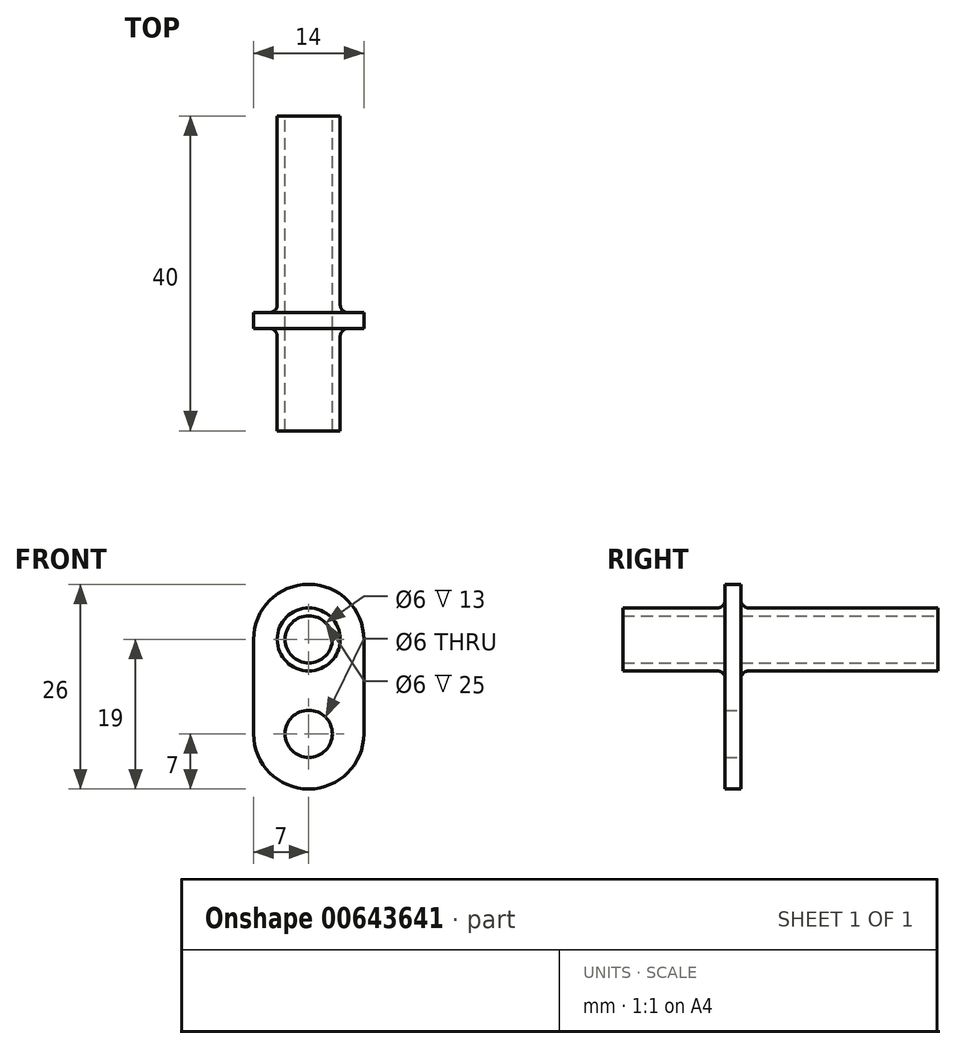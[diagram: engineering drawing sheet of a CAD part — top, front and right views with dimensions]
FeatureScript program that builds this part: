
annotation { "Feature Type Name" : "Feature", "Feature Type Description" : "" }
export const myFeature = defineFeature(function(context is Context, id is Id, definition is map)
    precondition{}
    {
        {
            var Q0;
            Q0=qCreatedBy(makeId("Front.planeOp"),FACE);
            var sketch = newSketch(context, id + "F0", { "sketchPlane" : qUnion([Q0])});
            skCircle(sketch, "E0", {"center": v(0, 0) * mm, "radius": 3 * mm});
            skCircle(sketch, "E1", {"center": v(0, 0) * mm, "radius": 4 * mm});
            skSolve(sketch);
        }
        {
            var Q0;
            Q0 = qSketchRegion(id + "F0", true);
            extrude(context, id + "F1", {"entities" : qUnion([Q0]), "depth" : 40 * mm, "offsetDistance" : 25 * mm});
        }
        {
            var Q0;
            Q0=qCreatedBy(makeId("Front.planeOp"),FACE);
            cPlane(context, id + "F2", {"entities" : qUnion([Q0]), "cplaneType" : CPlaneType.OFFSET, "offset" : 25 * mm, "width" : 150 * mm, "height" : 150 * mm});
        }
        {
            var Q0;
            Q0=qCreatedBy(id+"F2.planeOp",FACE);
            var sketch = newSketch(context, id + "F3", { "sketchPlane" : qUnion([Q0])});
            skCircle(sketch, "E2", {"center": v(0, -12) * mm, "radius": 3 * mm});
            skArc(sketch, "E3", {"start": v(-7, -12) * mm, "mid": v(0, -19) * mm, "end": v(7, -12) * mm});
            skArc(sketch, "E4", {"start": v(7, 0) * mm, "mid": v(0, 7) * mm, "end": v(-7, 0) * mm});
            skLineSegment(sketch, "E5", {"start": v(-7, 0) * mm, "end": v(7, 0) * mm, "construction": true});
            skLineSegment(sketch, "E6", {"start": v(-7, -12) * mm, "end": v(7, -12) * mm, "construction": true});
            skLineSegment(sketch, "E7", {"start": v(-7, 0) * mm, "end": v(-7, -12) * mm});
            skLineSegment(sketch, "E8", {"start": v(7, -12) * mm, "end": v(7, 0) * mm});
            skSolve(sketch);
        }
        {
            var Q0;
            Q0 = qSketchRegion(id + "F3", true);
            extrude(context, id + "F4", {"entities" : qUnion([Q0]), "operationType" : NewBodyOperationType.ADD, "depth" : 2 * mm, "offsetDistance" : 25 * mm});
        }
        {
            var Q0;
            Q0=makeQuery(id+"F4.boolean.opBoolean","INTERSECT",EDGE,{"derivedFrom":[makeQuery(id+"F1.opExtrude","SWEPT_FACE",FACE,{"disambiguationData":[OSD([sQuery(id+"F0.wireOp",EDGE,"E1")])]}),makeQuery(id+"F4.opExtrude","CAP_FACE",FACE,{"disambiguationData":[OSD([sQuery(id+"F3.wireOp",EDGE,"FZBSl5dX-5mwk-kPeC-qdXt-upEOPfOCjpsP"),sQuery(id+"F3.wireOp",EDGE,"8AeQqFBV-s7fN-LHIN-aBTI-KfVVdomFRjMM"),sQuery(id+"F3.wireOp",EDGE,"s0YkhkvZ-q8eN-i5ah-Za3n-ut8EPo8Zn2Ts"),sQuery(id+"F3.wireOp",EDGE,"R5PTpwiu-slRq-KExI-Zv77-W9f4wfKsHo7N"),sQuery(id+"F3.wireOp",EDGE,"E2")])],"isStart":false})]});
            var Q1;
            Q1=makeQuery(id+"F4.boolean.opBoolean","INTERSECT",EDGE,{"derivedFrom":[makeQuery(id+"F1.opExtrude","SWEPT_FACE",FACE,{"disambiguationData":[OSD([sQuery(id+"F0.wireOp",EDGE,"E1")])]}),makeQuery(id+"F4.opExtrude","CAP_FACE",FACE,{"disambiguationData":[OSD([sQuery(id+"F3.wireOp",EDGE,"FZBSl5dX-5mwk-kPeC-qdXt-upEOPfOCjpsP"),sQuery(id+"F3.wireOp",EDGE,"8AeQqFBV-s7fN-LHIN-aBTI-KfVVdomFRjMM"),sQuery(id+"F3.wireOp",EDGE,"s0YkhkvZ-q8eN-i5ah-Za3n-ut8EPo8Zn2Ts"),sQuery(id+"F3.wireOp",EDGE,"R5PTpwiu-slRq-KExI-Zv77-W9f4wfKsHo7N"),sQuery(id+"F3.wireOp",EDGE,"E2")])],"isStart":true})]});
            fillet(context, id + "F5", {"entities" : qUnion([Q0, Q1]), "radius" : 1 * mm, "tangentPropagation" : true, "allowEdgeOverflow" : false});
        }
    });
